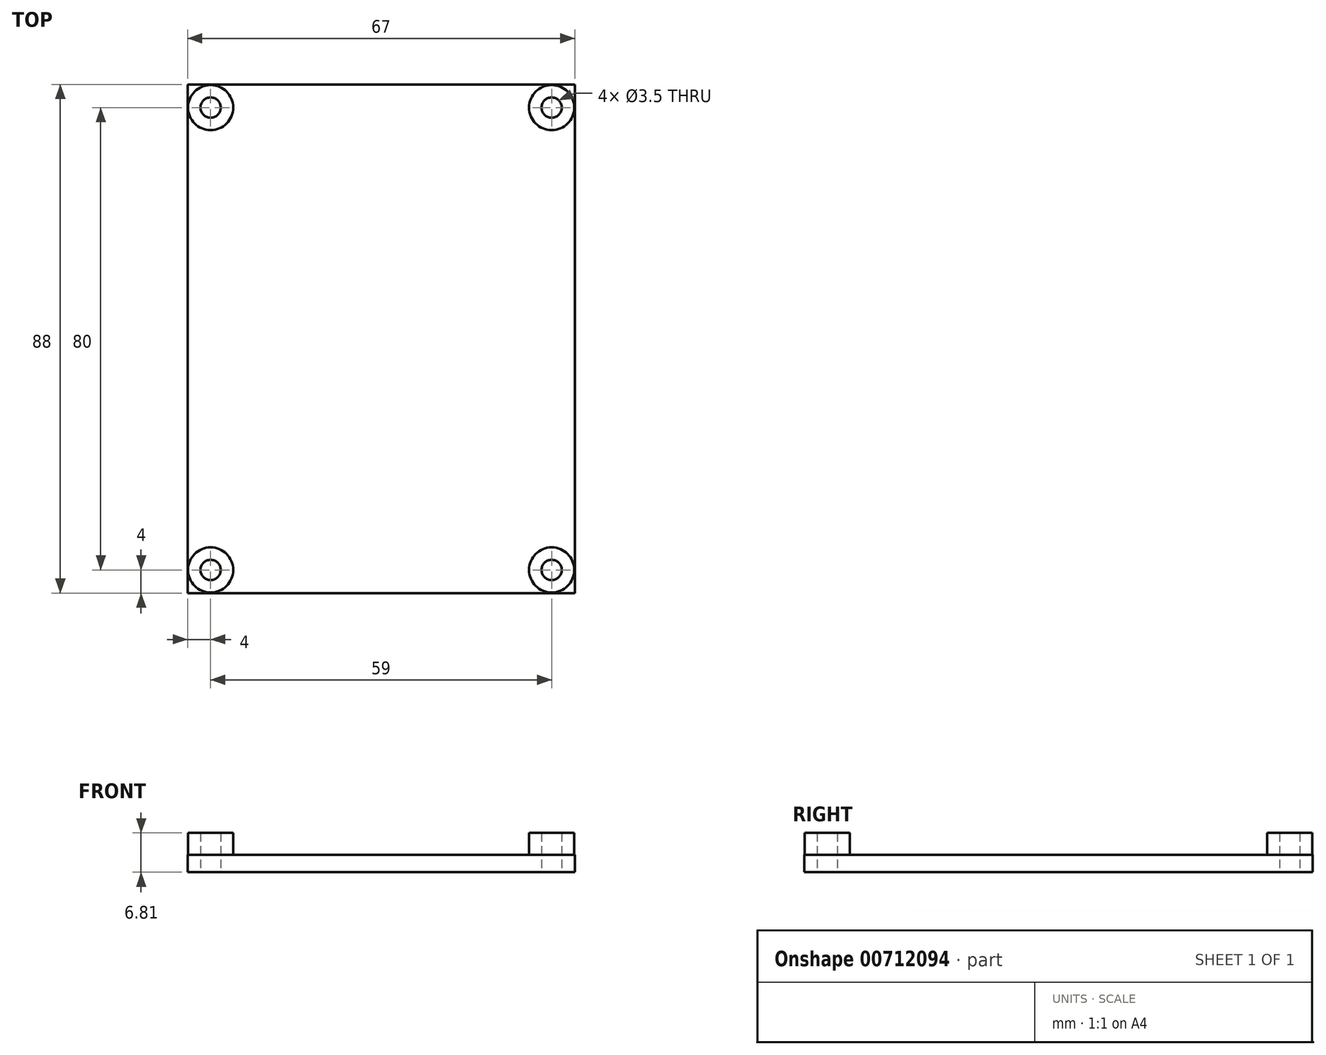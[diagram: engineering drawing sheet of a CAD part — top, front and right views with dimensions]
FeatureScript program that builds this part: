
annotation { "Feature Type Name" : "Feature", "Feature Type Description" : "" }
export const myFeature = defineFeature(function(context is Context, id is Id, definition is map)
    precondition{}
    {
        {
            var Q0;
            Q0=qCreatedBy(makeId("Top.planeOp"),FACE);
            var sketch = newSketch(context, id + "F0", { "sketchPlane" : qUnion([Q0])});
            skLineSegment(sketch, "E0.bottom", {"start": v(33.5, -44) * mm, "end": v(-33.5, -44) * mm});
            skLineSegment(sketch, "E0.top", {"start": v(33.5, 44) * mm, "end": v(-33.5, 44) * mm});
            skLineSegment(sketch, "E0.left", {"start": v(33.5, -44) * mm, "end": v(33.5, 44) * mm});
            skLineSegment(sketch, "E0.right", {"start": v(-33.5, -44) * mm, "end": v(-33.5, 44) * mm});
            skPoint(sketch, "E0.middle", {"position": v(0, 0) * mm});
            skSolve(sketch);
        }
        {
            var Q0;
            Q0 = qSketchRegion(id + "F0", true);
            extrude(context, id + "F1", {"entities" : qUnion([Q0]), "depth" : 3 * mm, "offsetDistance" : 25.4 * mm});
        }
        {
            var Q0;
            Q0=makeQuery(id+"F1.opExtrude","CAP_FACE",FACE,{"disambiguationData":[OSD([sQuery(id+"F0.wireOp",EDGE,"E0.bottom"),sQuery(id+"F0.wireOp",EDGE,"E0.top"),sQuery(id+"F0.wireOp",EDGE,"E0.left"),sQuery(id+"F0.wireOp",EDGE,"E0.right")])],"isStart":false});
            var sketch = newSketch(context, id + "F2", { "sketchPlane" : qUnion([Q0])});
            skCircle(sketch, "E1", {"center": v(-29.5, 40) * mm, "radius": 3.9 * mm});
            skLineSegment(sketch, "E2", {"start": v(0, 0) * mm, "end": v(0, 44) * mm, "construction": true});
            skLineSegment(sketch, "E3", {"start": v(0, 0) * mm, "end": v(-33.5, 0) * mm, "construction": true});
            skCircle(sketch, "E4.MirrorC", {"center": v(29.5, 40) * mm, "radius": 3.9 * mm});
            skCircle(sketch, "E5.MirrorC", {"center": v(-29.5, -40) * mm, "radius": 3.9 * mm});
            skCircle(sketch, "E6.MirrorC", {"center": v(29.5, -40) * mm, "radius": 3.9 * mm});
            skSolve(sketch);
        }
        {
            var Q0;
            Q0 = qSketchRegion(id + "F2", true);
            extrude(context, id + "F3", {"entities" : qUnion([Q0]), "operationType" : NewBodyOperationType.ADD, "depth" : 3.8 * mm, "offsetDistance" : 25.4 * mm});
        }
        {
            var Q0;
            Q0=makeQuery(id+"F1.opExtrude","CAP_FACE",FACE,{"disambiguationData":[OSD([sQuery(id+"F0.wireOp",EDGE,"E0.bottom"),sQuery(id+"F0.wireOp",EDGE,"E0.top"),sQuery(id+"F0.wireOp",EDGE,"E0.left"),sQuery(id+"F0.wireOp",EDGE,"E0.right")])],"isStart":true});
            var sketch = newSketch(context, id + "F4", { "sketchPlane" : qUnion([Q0])});
            skPoint(sketch, "E7", {"position": v(29.5, -40) * mm});
            skPoint(sketch, "E8", {"position": v(-29.5, -40) * mm});
            skPoint(sketch, "E9", {"position": v(-29.5, 40) * mm});
            skPoint(sketch, "E10", {"position": v(29.5, 40) * mm});
            skSolve(sketch);
        }
        {
            var Q0;
            Q0=sQuery(id+"F4.wireOp",VERTEX,"E10");
            var Q1;
            Q1=sQuery(id+"F4.wireOp",VERTEX,"E9");
            var Q2;
            Q2=sQuery(id+"F4.wireOp",VERTEX,"E8");
            var Q3;
            Q3=sQuery(id+"F4.wireOp",VERTEX,"E7");
            var Q4;
            Q4=makeQuery(id+"F1.opExtrude","SWEPT_BODY",BODY,{"disambiguationData":[OSD([sQuery(id+"F0.wireOp",EDGE,"E0.bottom"),sQuery(id+"F0.wireOp",EDGE,"E0.top"),sQuery(id+"F0.wireOp",EDGE,"E0.left"),sQuery(id+"F0.wireOp",EDGE,"E0.right")])]});
            hole(context, id + "F5", {"style" : HoleStyle.SIMPLE, "endStyle" : HoleEndStyle.THROUGH, "holeDiameter" : 3.5 * mm, "majorDiameter" : 6.35 * mm, "isTappedThrough" : true, "tappedDepth" : 12.7 * mm, "tapClearance" : 3, "locations" : qUnion([Q0, Q1, Q2, Q3]), "scope" : qUnion([Q4])});
        }
    });
